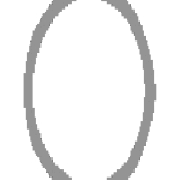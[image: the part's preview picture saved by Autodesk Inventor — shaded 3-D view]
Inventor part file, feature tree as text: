
AUTODESK INVENTOR PART (.ipt)
format: ipt  version: 2021 (Build 250183000, 183)  size: 113,664 bytes
history: native  units: in
note: dims shown in document units (in); Inventor stores cm internally (conversion verified against a paired STEP export)
features: other x4, sketch x3, plane x1
ambient origin geometry x8: Origin, YZ Plane, XZ Plane, XY Plane, X Axis, Y Axis, Z Axis, Center Point
bodies: Solid1 (feature_tree), Body (feature_tree)
feature tree (8):
  other  "Driven Length"
  other  "Frame Generator"
  other  "Start Plane"
  other  "End Plane"
  sketch  "Sketch"  dims[d2=3.5in d4=-0.0in d5=3.5in d6=0.12in d7=0.0in d8=90.0deg d9=3.5in]
  sketch  "Sketch2"  dims[d0=1.0in]
  plane  "Work Plane3"
  sketch  "Sketch3"  dims[d1=0.065in]
